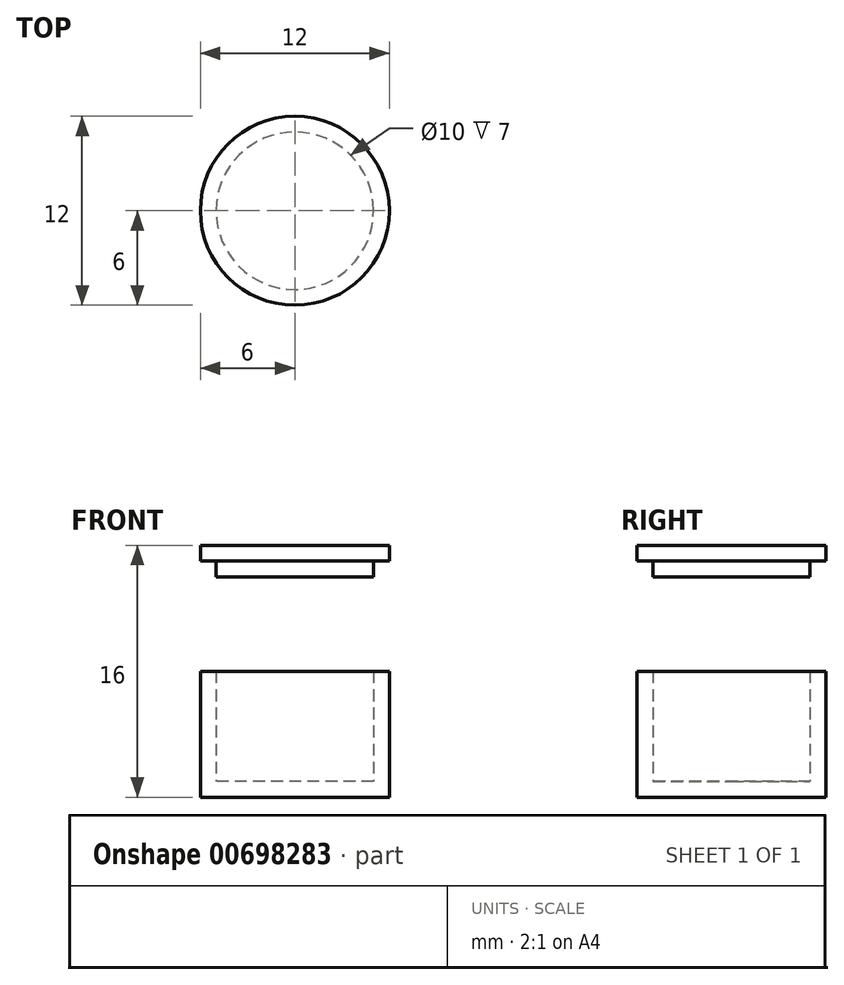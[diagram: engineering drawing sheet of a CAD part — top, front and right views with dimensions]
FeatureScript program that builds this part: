
annotation { "Feature Type Name" : "Feature", "Feature Type Description" : "" }
export const myFeature = defineFeature(function(context is Context, id is Id, definition is map)
    precondition{}
    {
        {
            var Q0;
            Q0=qCreatedBy(makeId("Top.planeOp"),FACE);
            var sketch = newSketch(context, id + "F0", { "sketchPlane" : qUnion([Q0])});
            skCircle(sketch, "E0", {"center": v(0, 0) * mm, "radius": 6 * mm});
            skSolve(sketch);
        }
        {
            var Q0;
            Q0=qSketchRegion(id+"F0",true);
            extrude(context, id + "F1", {"entities" : qUnion([Q0]), "depth" : 8 * mm, "offsetDistance" : 25 * mm});
        }
        {
            var Q0;
            Q0=makeQuery(id+"F1.opExtrude","CAP_FACE",FACE,{"disambiguationData":[OSD([sQuery(id+"F0.wireOp",EDGE,"E0")])],"isStart":false});
            shell(context, id + "F2", {"entities" : qUnion([Q0]), "thickness" : 1 * mm});
        }
        {
            var Q0;
            Q0=qCreatedBy(makeId("Top.planeOp"),FACE);
            cPlane(context, id + "F3", {"entities" : qUnion([Q0]), "cplaneType" : CPlaneType.OFFSET, "offset" : 15 * mm, "width" : 150 * mm, "height" : 150 * mm});
        }
        {
            var Q0;
            Q0=qCreatedBy(id+"F3.planeOp",FACE);
            var sketch = newSketch(context, id + "F4", { "sketchPlane" : qUnion([Q0])});
            skCircle(sketch, "E1.0", {"center": v(0, 0) * mm, "radius": 5 * mm});
            skCircle(sketch, "E2.0", {"center": v(0, 0) * mm, "radius": 6 * mm});
            skSolve(sketch);
        }
        {
            var Q0;
            Q0=makeQuery(id+"F4.imprint","IMPRINT",FACE,{"disambiguationData":[TD([[makeQuery(id+"F4.imprint","IMPRINT",EDGE,{"derivedFrom":sQuery(id+"F4.wireOp",EDGE,"E1.0")}),1.0]])]});
            extrude(context, id + "F5", {"entities" : qUnion([Q0]), "oppositeDirection" : true, "depth" : 1 * mm, "offsetDistance" : 25 * mm});
        }
        {
            var Q0;
            Q0=qSketchRegion(id+"F4",true);
            var Q1;
            Q1=makeQuery(id+"F5.opExtrude","CAP_FACE",FACE,{"disambiguationData":[OSD([sQuery(id+"F4.wireOp",EDGE,"E1.0")])],"isStart":true});
            extrude(context, id + "F6", {"entities" : qUnion([Q0, Q1]), "operationType" : NewBodyOperationType.ADD, "depth" : 1 * mm, "offsetDistance" : 25 * mm});
        }
    });
